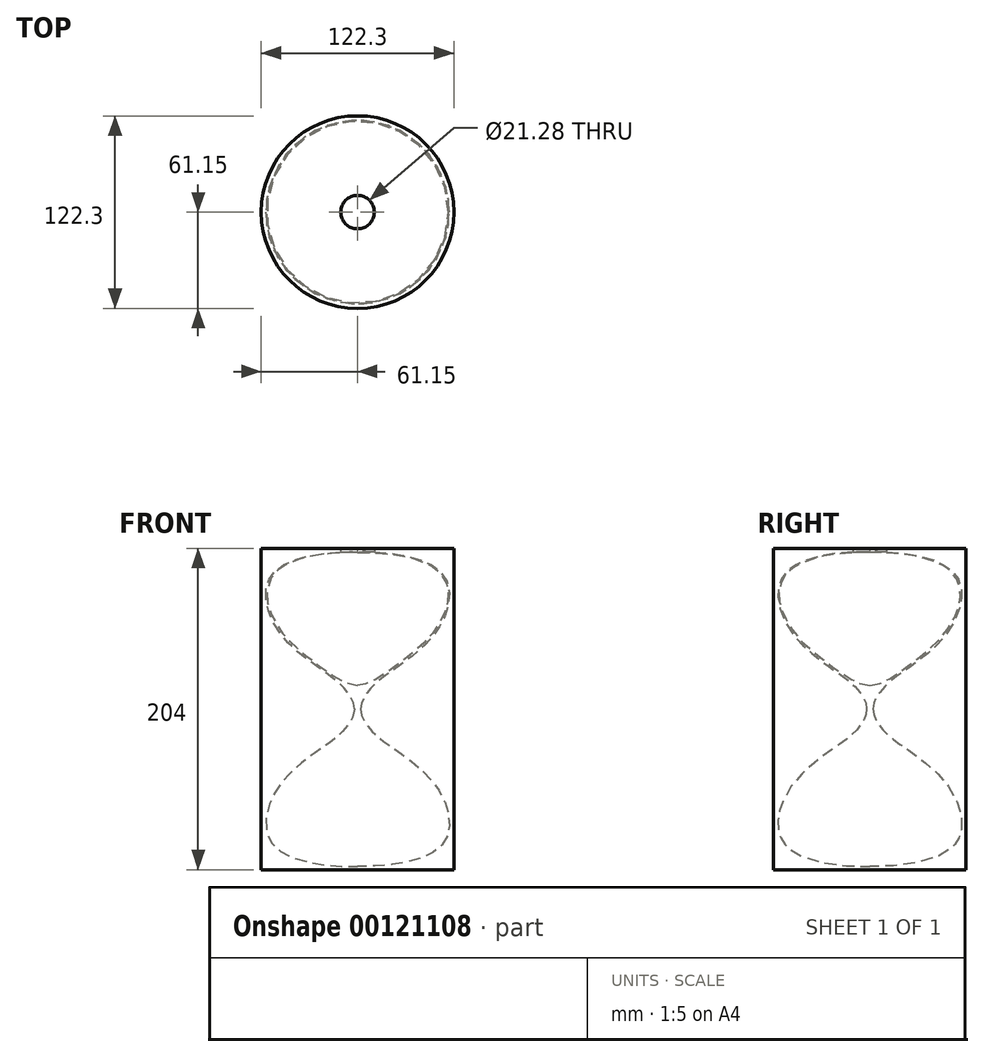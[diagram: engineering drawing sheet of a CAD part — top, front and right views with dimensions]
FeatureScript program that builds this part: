
annotation { "Feature Type Name" : "Feature", "Feature Type Description" : "" }
export const myFeature = defineFeature(function(context is Context, id is Id, definition is map)
    precondition{}
    {
        {
            var Q0;
            Q0=qCreatedBy(makeId("Front.planeOp"),FACE);
            var sketch = newSketch(context, id + "F0", { "sketchPlane" : qUnion([Q0])});
            skLineSegment(sketch, "E0", {"start": v(0, 0) * mm, "end": v(0, 100) * mm});
            skLineSegment(sketch, "E1", {"start": v(0, 0) * mm, "end": v(80.48, 0) * mm});
            skFitSpline(sketch, "E2", {"points": [v(2, 0) * mm, v(6.17, 10.46) * mm, v(16.7, 20.51) * mm, v(49.7, 48.77) * mm, v(55.06, 84.46) * mm, v(0, 100) * mm], "startDerivative": vector(0.36, 99.1) * mm, "endDerivative": vector(-258.3, -0.4) * mm});
            skLineSegment(sketch, "E3", {"start": v(0, 100) * mm, "end": v(0, 102) * mm});
            skLineSegment(sketch, "E4", {"start": v(0, 102) * mm, "end": v(61.15, 102) * mm});
            skLineSegment(sketch, "E5", {"start": v(61.15, 102) * mm, "end": v(61.15, 0) * mm});
            skLineSegment(sketch, "E6.MirrorCS", {"start": v(61.15, -102) * mm, "end": v(61.15, 0) * mm});
            skLineSegment(sketch, "E7.MirrorCS", {"start": v(0, -102) * mm, "end": v(61.15, -102) * mm});
            skFitSpline(sketch, "E8.MirrorCS", {"points": [v(2, 0) * mm, v(6.17, -10.46) * mm, v(16.7, -20.51) * mm, v(49.7, -48.77) * mm, v(55.06, -84.46) * mm, v(0, -100) * mm], "startDerivative": vector(0.36, -99.1) * mm, "endDerivative": vector(-258.3, 0.4) * mm});
            skLineSegment(sketch, "E9.MirrorCS", {"start": v(0, -102) * mm, "end": v(-61.15, -102) * mm});
            skLineSegment(sketch, "E10.MirrorCS", {"start": v(-61.15, -102) * mm, "end": v(-61.15, 0) * mm});
            skFitSpline(sketch, "E11.MirrorCS", {"points": [v(-2, 0) * mm, v(-6.17, -10.46) * mm, v(-16.7, -20.51) * mm, v(-49.7, -48.77) * mm, v(-55.06, -84.46) * mm, v(0, -100) * mm], "startDerivative": vector(-0.36, -99.1) * mm, "endDerivative": vector(258.3, 0.4) * mm});
            skFitSpline(sketch, "E12.MirrorCS", {"points": [v(-2, 0) * mm, v(-6.17, 10.46) * mm, v(-16.7, 20.51) * mm, v(-49.7, 48.77) * mm, v(-55.06, 84.46) * mm, v(0, 100) * mm], "startDerivative": vector(-0.36, 99.1) * mm, "endDerivative": vector(258.3, -0.4) * mm});
            skLineSegment(sketch, "E13.MirrorCS", {"start": v(0, 102) * mm, "end": v(-61.15, 102) * mm});
            skLineSegment(sketch, "E14.MirrorCS", {"start": v(-61.15, 102) * mm, "end": v(-61.15, 0) * mm});
            skLineSegment(sketch, "E15", {"start": v(0, -100) * mm, "end": v(0, -102) * mm});
            skLineSegment(sketch, "E16", {"start": v(10.64, 99.75) * mm, "end": v(10.64, 102) * mm});
            skFitSpline(sketch, "E17", {"points": [v(0, 99.62) * mm, v(4.28, 99.53) * mm, v(10.64, 99.27) * mm, v(18.57, 98.67) * mm, v(27.9, 97.38) * mm, v(38.04, 94.74) * mm, v(46.37, 91.23) * mm, v(54.44, 84.04) * mm, v(57.47, 75.05) * mm, v(57.25, 67.94) * mm, v(54.34, 59.36) * mm, v(46.66, 46.85) * mm, v(37.01, 37.5) * mm, v(26.38, 28.93) * mm, v(15.58, 21.25) * mm, v(6.12, 16.17) * mm, v(0, 15.07) * mm], "startDerivative": vector(97.5, -1.8) * mm, "endDerivative": vector(-116.5, -10.36) * mm});
            skFitSpline(sketch, "E18.MirrorCS", {"points": [v(0, 99.62) * mm, v(-4.28, 99.53) * mm, v(-10.64, 99.27) * mm, v(-18.57, 98.67) * mm, v(-27.9, 97.38) * mm, v(-38.04, 94.74) * mm, v(-46.37, 91.23) * mm, v(-54.44, 84.04) * mm, v(-57.47, 75.05) * mm, v(-57.25, 67.94) * mm, v(-54.34, 59.36) * mm, v(-46.66, 46.85) * mm, v(-37.01, 37.5) * mm, v(-26.38, 28.93) * mm, v(-15.58, 21.25) * mm, v(-6.12, 16.17) * mm, v(0, 15.07) * mm], "startDerivative": vector(-97.5, -1.8) * mm, "endDerivative": vector(116.5, -10.36) * mm});
            skSolve(sketch);
        }
        {
            var Q0;
            {var subQ0=sQuery(id+"F0.wireOp",EDGE,"E5");Q0=makeQuery(id+"F0.imprint","IMPRINT",FACE,{"disambiguationData":[TD([[makeQuery(id+"F0.imprint","IMPRINT",EDGE,{"derivedFrom":subQ0}),-1.0]])]});}
            var Q1;
            {var subQ1=sQuery(id+"F0.wireOp",EDGE,"E8.MirrorCS");Q1=makeQuery(id+"F0.imprint","IMPRINT",FACE,{"disambiguationData":[TD([[makeQuery(id+"F0.imprint","IMPRINT",EDGE,{"derivedFrom":subQ1}),1.0]])]});}
            var Q2;
            Q2=sQuery(id+"F0.wireOp",EDGE,"E0");
            revolve(context, id + "F1", {"entities" : qUnion([Q0, Q1]), "axis" : qUnion([Q2]), "revolveType" : RevolveType.FULL});
        }
        {
            var Q0;
            {var subQ0=sQuery(id+"F0.wireOp",EDGE,"E3");Q0=makeQuery(id+"F0.imprint","IMPRINT",FACE,{"disambiguationData":[TD([[makeQuery(id+"F0.imprint","IMPRINT",EDGE,{"derivedFrom":subQ0}),-1.0]])]});}
            var Q1;
            Q1=sQuery(id+"F0.wireOp",EDGE,"E0");
            revolve(context, id + "F2", {"entities" : qUnion([Q0]), "axis" : qUnion([Q1]), "revolveType" : RevolveType.FULL});
        }
        {
            var Q0;
            {var subQ1=sQuery(id+"F0.wireOp",EDGE,"E17");Q0=makeQuery(id+"F0.imprint","IMPRINT",FACE,{"disambiguationData":[TD([[makeQuery(id+"F0.imprint","IMPRINT",EDGE,{"derivedFrom":subQ1}),-1.0]])]});}
            var Q1;
            Q1=sQuery(id+"F0.wireOp",EDGE,"E0");
            revolve(context, id + "F3", {"entities" : qUnion([Q0]), "axis" : qUnion([Q1]), "revolveType" : RevolveType.FULL});
        }
    });
